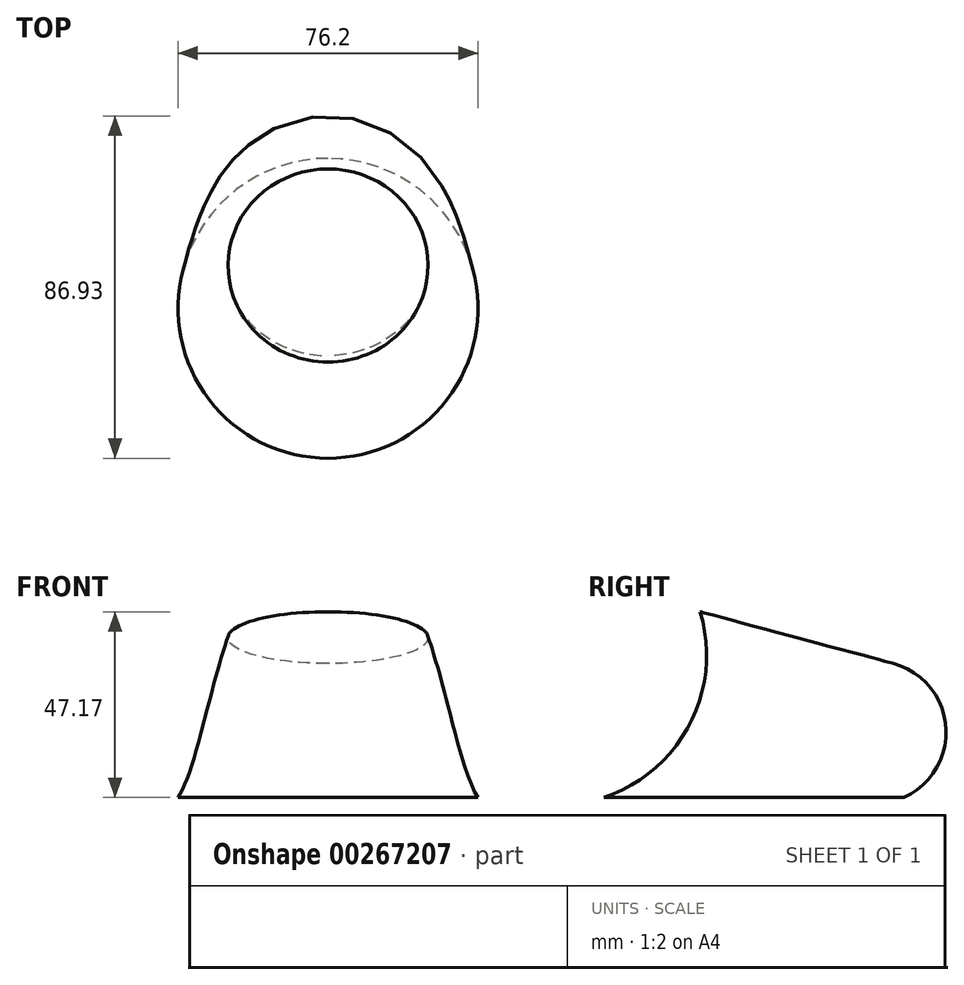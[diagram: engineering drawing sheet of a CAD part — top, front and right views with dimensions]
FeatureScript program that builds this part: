
annotation { "Feature Type Name" : "Feature", "Feature Type Description" : "" }
export const myFeature = defineFeature(function(context is Context, id is Id, definition is map)
    precondition{}
    {
        {
            var Q0;
            Q0=qCreatedBy(makeId("Top.planeOp"),FACE);
            var sketch = newSketch(context, id + "F0", { "sketchPlane" : qUnion([Q0])});
            skCircle(sketch, "E0", {"center": v(0, 0) * mm, "radius": 38.1 * mm});
            skLineSegment(sketch, "E1", {"start": v(-63.5, 64.25) * mm, "end": v(63.5, 64.25) * mm});
            skSolve(sketch);
        }
        {
            var Q0;
            Q0=sQuery(id+"F0.wireOp",EDGE,"E1");
            cPlane(context, id + "F1", {"entities" : qUnion([Q0]), "cplaneType" : CPlaneType.LINE_ANGLE, "offset" : 25.4 * mm, "angle" : 75 * degree, "width" : 152.4 * mm, "height" : 152.4 * mm});
        }
        {
            var Q0;
            Q0=qCreatedBy(id+"F1.planeOp",FACE);
            cPlane(context, id + "F2", {"entities" : qUnion([Q0]), "cplaneType" : CPlaneType.OFFSET, "offset" : 25.4 * mm, "width" : 152.4 * mm, "height" : 152.4 * mm});
        }
        {
            var Q0;
            Q0=qCreatedBy(id+"F2.planeOp",FACE);
            var sketch = newSketch(context, id + "F3", { "sketchPlane" : qUnion([Q0])});
            skCircle(sketch, "E2", {"center": v(0, 0) * mm, "radius": 25.4 * mm});
            skSolve(sketch);
        }
        {
            var Q0;
            Q0=qCreatedBy(makeId("Right.planeOp"),FACE);
            var sketch = newSketch(context, id + "F4", { "sketchPlane" : qUnion([Q0])});
            skLineSegment(sketch, "E3.0", {"start": v(-13.66, 47.17) * mm, "end": v(35.41, 34.02) * mm});
            skLineSegment(sketch, "E3.1", {"start": v(-38.1, 0) * mm, "end": v(38.1, 0) * mm});
            skArc(sketch, "E4", {"start": v(-38.1, 0) * mm, "mid": v(-16.3, 18.62) * mm, "end": v(-13.66, 47.17) * mm});
            skArc(sketch, "E5", {"start": v(35.41, 34.02) * mm, "mid": v(48.78, 17.96) * mm, "end": v(38.1, 0) * mm});
            skSolve(sketch);
        }
        {
            var Q0;
            Q0=makeQuery(id+"F0.imprint","IMPRINT",FACE,{"disambiguationData":[TD([[makeQuery(id+"F0.imprint","IMPRINT",EDGE,{"derivedFrom":sQuery(id+"F0.wireOp",EDGE,"E0")}),1.0]])]});
            var Q1;
            Q1=makeQuery(id+"F3.imprint","IMPRINT",FACE,{"disambiguationData":[TD([[makeQuery(id+"F3.imprint","IMPRINT",EDGE,{"derivedFrom":sQuery(id+"F3.wireOp",EDGE,"E2")}),1.0]])]});
            var Q2;
            Q2=sQuery(id+"F4.wireOp",EDGE,"E4");
            var Q3;
            Q3=sQuery(id+"F4.wireOp",EDGE,"E5");
            loft(context, id + "F5", {"addGuides" : true, "sheetProfilesArray" : [{ "sheetProfileEntities" : qUnion([Q0]) }, { "sheetProfileEntities" : qUnion([Q1]) }], "guidesArray" : [{ "guideEntities" : qUnion([Q2]), "guideDerivativeType" : LoftGuideDerivativeType.DEFAULT, "guideDerivativeMagnitude" : 1 }, { "guideEntities" : qUnion([Q3]), "guideDerivativeType" : LoftGuideDerivativeType.DEFAULT, "guideDerivativeMagnitude" : 1 }]});
        }
    });
